# Revit family: Legrand_Atlantic_versione_verticale_riferimenti_036910_a_036950
name_source: partatom
category: Installations électriques
revit_build: Autodesk Revit 2018 (Build: 20170223_1515(x64)
units: mm (PartAtom-declared; Revit-internal decimal feet)

## family parameters
Basée sur le plan de construction = Non
Conserver l'orientation des annotations = Non
Cote de connecteur circulaire = Utiliser le diamètre
Couper avec des vides une fois chargée = Non
Numéro OmniClass = 23.80.00.00
Partagée = Non
Point de calcul de pièce = Non
Titre OmniClass = Electric Power and Lighting
Toujours verticalement = Oui
Type d'élément = Normal

## types (23) — shared parameters
Condizioni Generali di Utilizzo = https://export.legrand.com
ETIM Class 6.0 = EC000058
Fabricant = Legrand
IK = 10
IP = 66
RAL = 7035
URL = www.legrand.fr
materiale = metallo
numero di porte = 1
versione orizzontale = Non
versione quadrata = Non
versione verticale = Oui

## per-type parameters (varying)
- Legrand Atlantic 036913: Scatola 036910=Non; Scatola 036912=Non; Scatola 036913=Oui; Scatola 036917=Non; Scatola 036918=Non; Scatola 036919=Non; Scatola 036920=Non; Scatola 036921=Non; Scatola 036925=Non; Scatola 036926=Non; Scatola 036930=Non; Scatola 036931=Non; Scatola 036932=Non; Scatola 036933=Non; Scatola 036937=Non; Scatola 036938=Non; Scatola 036939=Non; Scatola 036942=Non; Scatola 036943=Non; Scatola 036944=Non; Scatola 036945=Non; Scatola 036946=Non; Scatola 036950=Non; altezza=500 mm  [stored 1.64042 ft]; lunghezza=400 mm  [stored 1.31234 ft]; peso=9.70 kg; profondità=160 mm  [stored 0.524934 ft]
- Legrand Atlantic 036920: Scatola 036910=Non; Scatola 036912=Non; Scatola 036913=Non; Scatola 036917=Non; Scatola 036918=Non; Scatola 036919=Non; Scatola 036920=Oui; Scatola 036921=Non; Scatola 036925=Non; Scatola 036926=Non; Scatola 036930=Non; Scatola 036931=Non; Scatola 036932=Non; Scatola 036933=Non; Scatola 036937=Non; Scatola 036938=Non; Scatola 036939=Non; Scatola 036942=Non; Scatola 036943=Non; Scatola 036944=Non; Scatola 036945=Non; Scatola 036946=Non; Scatola 036950=Non; altezza=600 mm; lunghezza=500 mm  [stored 1.64042 ft]; peso=16.60 kg; profondità=200 mm  [stored 0.656168 ft]
- Legrand Atlantic 036921: Scatola 036910=Non; Scatola 036912=Non; Scatola 036913=Non; Scatola 036917=Non; Scatola 036918=Non; Scatola 036919=Non; Scatola 036920=Non; Scatola 036921=Oui; Scatola 036925=Non; Scatola 036926=Non; Scatola 036930=Non; Scatola 036931=Non; Scatola 036932=Non; Scatola 036933=Non; Scatola 036937=Non; Scatola 036938=Non; Scatola 036939=Non; Scatola 036942=Non; Scatola 036943=Non; Scatola 036944=Non; Scatola 036945=Non; Scatola 036946=Non; Scatola 036950=Non; altezza=700 mm  [stored 2.29659 ft]; lunghezza=500 mm  [stored 1.64042 ft]; peso=18.40 kg; profondità=200 mm  [stored 0.656168 ft]
- Legrand Atlantic 036942: Scatola 036910=Non; Scatola 036912=Non; Scatola 036913=Non; Scatola 036917=Non; Scatola 036918=Non; Scatola 036919=Non; Scatola 036920=Non; Scatola 036921=Non; Scatola 036925=Non; Scatola 036926=Non; Scatola 036930=Non; Scatola 036931=Non; Scatola 036932=Non; Scatola 036933=Non; Scatola 036937=Non; Scatola 036938=Non; Scatola 036939=Non; Scatola 036942=Oui; Scatola 036943=Non; Scatola 036944=Non; Scatola 036945=Non; Scatola 036946=Non; Scatola 036950=Non; altezza=1200 mm; lunghezza=600 mm; peso=47.00 kg; profondità=300 mm
- Legrand Atlantic 036910: Scatola 036910=Oui; Scatola 036912=Non; Scatola 036913=Non; Scatola 036917=Non; Scatola 036918=Non; Scatola 036919=Non; Scatola 036920=Non; Scatola 036921=Non; Scatola 036925=Non; Scatola 036926=Non; Scatola 036930=Non; Scatola 036931=Non; Scatola 036932=Non; Scatola 036933=Non; Scatola 036937=Non; Scatola 036938=Non; Scatola 036939=Non; Scatola 036942=Non; Scatola 036943=Non; Scatola 036944=Non; Scatola 036945=Non; Scatola 036946=Non; Scatola 036950=Non; altezza=300 mm; lunghezza=200 mm  [stored 0.656168 ft]; peso=3.70 kg; profondità=160 mm  [stored 0.524934 ft]
- Legrand Atlantic 036912: Scatola 036910=Non; Scatola 036912=Oui; Scatola 036913=Non; Scatola 036917=Non; Scatola 036918=Non; Scatola 036919=Non; Scatola 036920=Non; Scatola 036921=Non; Scatola 036925=Non; Scatola 036926=Non; Scatola 036930=Non; Scatola 036931=Non; Scatola 036932=Non; Scatola 036933=Non; Scatola 036937=Non; Scatola 036938=Non; Scatola 036939=Non; Scatola 036942=Non; Scatola 036943=Non; Scatola 036944=Non; Scatola 036945=Non; Scatola 036946=Non; Scatola 036950=Non; altezza=400 mm  [stored 1.31234 ft]; lunghezza=300 mm; peso=6.30 kg; profondità=160 mm  [stored 0.524934 ft]
- Legrand Atlantic 036917: Scatola 036910=Non; Scatola 036912=Non; Scatola 036913=Non; Scatola 036917=Oui; Scatola 036918=Non; Scatola 036919=Non; Scatola 036920=Non; Scatola 036921=Non; Scatola 036925=Non; Scatola 036926=Non; Scatola 036930=Non; Scatola 036931=Non; Scatola 036932=Non; Scatola 036933=Non; Scatola 036937=Non; Scatola 036938=Non; Scatola 036939=Non; Scatola 036942=Non; Scatola 036943=Non; Scatola 036944=Non; Scatola 036945=Non; Scatola 036946=Non; Scatola 036950=Non; altezza=400 mm  [stored 1.31234 ft]; lunghezza=300 mm; peso=6.70 kg; profondità=200 mm  [stored 0.656168 ft]
- Legrand Atlantic 036918: Scatola 036910=Non; Scatola 036912=Non; Scatola 036913=Non; Scatola 036917=Non; Scatola 036918=Oui; Scatola 036919=Non; Scatola 036920=Non; Scatola 036921=Non; Scatola 036925=Non; Scatola 036926=Non; Scatola 036930=Non; Scatola 036931=Non; Scatola 036932=Non; Scatola 036933=Non; Scatola 036937=Non; Scatola 036938=Non; Scatola 036939=Non; Scatola 036942=Non; Scatola 036943=Non; Scatola 036944=Non; Scatola 036945=Non; Scatola 036946=Non; Scatola 036950=Non; altezza=500 mm  [stored 1.64042 ft]; lunghezza=400 mm  [stored 1.31234 ft]; peso=10.60 kg; profondità=160 mm  [stored 0.524934 ft]
- Legrand Atlantic 036919: Scatola 036910=Non; Scatola 036912=Non; Scatola 036913=Non; Scatola 036917=Non; Scatola 036918=Non; Scatola 036919=Oui; Scatola 036920=Non; Scatola 036921=Non; Scatola 036925=Non; Scatola 036926=Non; Scatola 036930=Non; Scatola 036931=Non; Scatola 036932=Non; Scatola 036933=Non; Scatola 036937=Non; Scatola 036938=Non; Scatola 036939=Non; Scatola 036942=Non; Scatola 036943=Non; Scatola 036944=Non; Scatola 036945=Non; Scatola 036946=Non; Scatola 036950=Non; altezza=600 mm; lunghezza=400 mm  [stored 1.31234 ft]; peso=12.00 kg; profondità=160 mm  [stored 0.524934 ft]
- Legrand Atlantic 036925: Scatola 036910=Non; Scatola 036912=Non; Scatola 036913=Non; Scatola 036917=Non; Scatola 036918=Non; Scatola 036919=Non; Scatola 036920=Non; Scatola 036921=Non; Scatola 036925=Oui; Scatola 036926=Non; Scatola 036930=Non; Scatola 036931=Non; Scatola 036932=Non; Scatola 036933=Non; Scatola 036937=Non; Scatola 036938=Non; Scatola 036939=Non; Scatola 036942=Non; Scatola 036943=Non; Scatola 036944=Non; Scatola 036945=Non; Scatola 036946=Non; Scatola 036950=Non; altezza=500 mm  [stored 1.64042 ft]; lunghezza=400 mm  [stored 1.31234 ft]; peso=11.30 kg; profondità=250 mm  [stored 0.82021 ft]
- Legrand Atlantic 036926: Scatola 036910=Non; Scatola 036912=Non; Scatola 036913=Non; Scatola 036917=Non; Scatola 036918=Non; Scatola 036919=Non; Scatola 036920=Non; Scatola 036921=Non; Scatola 036925=Non; Scatola 036926=Oui; Scatola 036930=Non; Scatola 036931=Non; Scatola 036932=Non; Scatola 036933=Non; Scatola 036937=Non; Scatola 036938=Non; Scatola 036939=Non; Scatola 036942=Non; Scatola 036943=Non; Scatola 036944=Non; Scatola 036945=Non; Scatola 036946=Non; Scatola 036950=Non; altezza=500 mm  [stored 1.64042 ft]; lunghezza=400 mm  [stored 1.31234 ft]; peso=12.80 kg; profondità=250 mm  [stored 0.82021 ft]
- Legrand Atlantic 036930: Scatola 036910=Non; Scatola 036912=Non; Scatola 036913=Non; Scatola 036917=Non; Scatola 036918=Non; Scatola 036919=Non; Scatola 036920=Non; Scatola 036921=Non; Scatola 036925=Non; Scatola 036926=Non; Scatola 036930=Oui; Scatola 036931=Non; Scatola 036932=Non; Scatola 036933=Non; Scatola 036937=Non; Scatola 036938=Non; Scatola 036939=Non; Scatola 036942=Non; Scatola 036943=Non; Scatola 036944=Non; Scatola 036945=Non; Scatola 036946=Non; Scatola 036950=Non; altezza=700 mm  [stored 2.29659 ft]; lunghezza=500 mm  [stored 1.64042 ft]; peso=19.60 kg; profondità=250 mm  [stored 0.82021 ft]
- Legrand Atlantic 036931: Scatola 036910=Non; Scatola 036912=Non; Scatola 036913=Non; Scatola 036917=Non; Scatola 036918=Non; Scatola 036919=Non; Scatola 036920=Non; Scatola 036921=Non; Scatola 036925=Non; Scatola 036926=Non; Scatola 036930=Non; Scatola 036931=Oui; Scatola 036932=Non; Scatola 036933=Non; Scatola 036937=Non; Scatola 036938=Non; Scatola 036939=Non; Scatola 036942=Non; Scatola 036943=Non; Scatola 036944=Non; Scatola 036945=Non; Scatola 036946=Non; Scatola 036950=Non; altezza=800 mm  [stored 2.62467 ft]; lunghezza=600 mm; peso=26.60 kg; profondità=250 mm  [stored 0.82021 ft]
- Legrand Atlantic 036932: Scatola 036910=Non; Scatola 036912=Non; Scatola 036913=Non; Scatola 036917=Non; Scatola 036918=Non; Scatola 036919=Non; Scatola 036920=Non; Scatola 036921=Non; Scatola 036925=Non; Scatola 036926=Non; Scatola 036930=Non; Scatola 036931=Non; Scatola 036932=Oui; Scatola 036933=Non; Scatola 036937=Non; Scatola 036938=Non; Scatola 036939=Non; Scatola 036942=Non; Scatola 036943=Non; Scatola 036944=Non; Scatola 036945=Non; Scatola 036946=Non; Scatola 036950=Non; altezza=1000 mm  [stored 3.28084 ft]; lunghezza=600 mm; peso=36.20 kg; profondità=250 mm  [stored 0.82021 ft]
- Legrand Atlantic 036933: Scatola 036910=Non; Scatola 036912=Non; Scatola 036913=Non; Scatola 036917=Non; Scatola 036918=Non; Scatola 036919=Non; Scatola 036920=Non; Scatola 036921=Non; Scatola 036925=Non; Scatola 036926=Non; Scatola 036930=Non; Scatola 036931=Non; Scatola 036932=Non; Scatola 036933=Oui; Scatola 036937=Non; Scatola 036938=Non; Scatola 036939=Non; Scatola 036942=Non; Scatola 036943=Non; Scatola 036944=Non; Scatola 036945=Non; Scatola 036946=Non; Scatola 036950=Non; altezza=1000 mm  [stored 3.28084 ft]; lunghezza=800 mm  [stored 2.62467 ft]; peso=46.80 kg; profondità=250 mm  [stored 0.82021 ft]
- Legrand Atlantic 036937: Scatola 036910=Non; Scatola 036912=Non; Scatola 036913=Non; Scatola 036917=Non; Scatola 036918=Non; Scatola 036919=Non; Scatola 036920=Non; Scatola 036921=Non; Scatola 036925=Non; Scatola 036926=Non; Scatola 036930=Non; Scatola 036931=Non; Scatola 036932=Non; Scatola 036933=Non; Scatola 036937=Oui; Scatola 036938=Non; Scatola 036939=Non; Scatola 036942=Non; Scatola 036943=Non; Scatola 036944=Non; Scatola 036945=Non; Scatola 036946=Non; Scatola 036950=Non; altezza=800 mm  [stored 2.62467 ft]; lunghezza=600 mm; peso=28.80 kg; profondità=300 mm
- Legrand Atlantic 036938: Scatola 036910=Non; Scatola 036912=Non; Scatola 036913=Non; Scatola 036917=Non; Scatola 036918=Non; Scatola 036919=Non; Scatola 036920=Non; Scatola 036921=Non; Scatola 036925=Non; Scatola 036926=Non; Scatola 036930=Non; Scatola 036931=Non; Scatola 036932=Non; Scatola 036933=Non; Scatola 036937=Non; Scatola 036938=Oui; Scatola 036939=Non; Scatola 036942=Non; Scatola 036943=Non; Scatola 036944=Non; Scatola 036945=Non; Scatola 036946=Non; Scatola 036950=Non; altezza=1000 mm  [stored 3.28084 ft]; lunghezza=600 mm; peso=37.80 kg; profondità=300 mm
- Legrand Atlantic 036939: Scatola 036910=Non; Scatola 036912=Non; Scatola 036913=Non; Scatola 036917=Non; Scatola 036918=Non; Scatola 036919=Non; Scatola 036920=Non; Scatola 036921=Non; Scatola 036925=Non; Scatola 036926=Non; Scatola 036930=Non; Scatola 036931=Non; Scatola 036932=Non; Scatola 036933=Non; Scatola 036937=Non; Scatola 036938=Non; Scatola 036939=Oui; Scatola 036942=Non; Scatola 036943=Non; Scatola 036944=Non; Scatola 036945=Non; Scatola 036946=Non; Scatola 036950=Non; altezza=1000 mm  [stored 3.28084 ft]; lunghezza=800 mm  [stored 2.62467 ft]; peso=50.50 kg; profondità=300 mm
- Legrand Atlantic 036943: Scatola 036910=Non; Scatola 036912=Non; Scatola 036913=Non; Scatola 036917=Non; Scatola 036918=Non; Scatola 036919=Non; Scatola 036920=Non; Scatola 036921=Non; Scatola 036925=Non; Scatola 036926=Non; Scatola 036930=Non; Scatola 036931=Non; Scatola 036932=Non; Scatola 036933=Non; Scatola 036937=Non; Scatola 036938=Non; Scatola 036939=Non; Scatola 036942=Non; Scatola 036943=Oui; Scatola 036944=Non; Scatola 036945=Non; Scatola 036946=Non; Scatola 036950=Non; altezza=1200 mm; lunghezza=800 mm  [stored 2.62467 ft]; peso=62.20 kg; profondità=300 mm
- Legrand Atlantic 036944: Scatola 036910=Non; Scatola 036912=Non; Scatola 036913=Non; Scatola 036917=Non; Scatola 036918=Non; Scatola 036919=Non; Scatola 036920=Non; Scatola 036921=Non; Scatola 036925=Non; Scatola 036926=Non; Scatola 036930=Non; Scatola 036931=Non; Scatola 036932=Non; Scatola 036933=Non; Scatola 036937=Non; Scatola 036938=Non; Scatola 036939=Non; Scatola 036942=Non; Scatola 036943=Non; Scatola 036944=Oui; Scatola 036945=Non; Scatola 036946=Non; Scatola 036950=Non; altezza=800 mm  [stored 2.62467 ft]; lunghezza=600 mm; peso=36.80 kg; profondità=400 mm  [stored 1.31234 ft]
- Legrand Atlantic 036945: Scatola 036910=Non; Scatola 036912=Non; Scatola 036913=Non; Scatola 036917=Non; Scatola 036918=Non; Scatola 036919=Non; Scatola 036920=Non; Scatola 036921=Non; Scatola 036925=Non; Scatola 036926=Non; Scatola 036930=Non; Scatola 036931=Non; Scatola 036932=Non; Scatola 036933=Non; Scatola 036937=Non; Scatola 036938=Non; Scatola 036939=Non; Scatola 036942=Non; Scatola 036943=Non; Scatola 036944=Non; Scatola 036945=Oui; Scatola 036946=Non; Scatola 036950=Non; altezza=1000 mm  [stored 3.28084 ft]; lunghezza=800 mm  [stored 2.62467 ft]; peso=62.30 kg; profondità=400 mm  [stored 1.31234 ft]
- Legrand Atlantic 036946: Scatola 036910=Non; Scatola 036912=Non; Scatola 036913=Non; Scatola 036917=Non; Scatola 036918=Non; Scatola 036919=Non; Scatola 036920=Non; Scatola 036921=Non; Scatola 036925=Non; Scatola 036926=Non; Scatola 036930=Non; Scatola 036931=Non; Scatola 036932=Non; Scatola 036933=Non; Scatola 036937=Non; Scatola 036938=Non; Scatola 036939=Non; Scatola 036942=Non; Scatola 036943=Non; Scatola 036944=Non; Scatola 036945=Non; Scatola 036946=Oui; Scatola 036950=Non; altezza=1200 mm; lunghezza=800 mm  [stored 2.62467 ft]; peso=76.00 kg; profondità=400 mm  [stored 1.31234 ft]
- Legrand Atlantic 036950: Scatola 036910=Non; Scatola 036912=Non; Scatola 036913=Non; Scatola 036917=Non; Scatola 036918=Non; Scatola 036919=Non; Scatola 036920=Non; Scatola 036921=Non; Scatola 036925=Non; Scatola 036926=Non; Scatola 036930=Non; Scatola 036931=Non; Scatola 036932=Non; Scatola 036933=Non; Scatola 036937=Non; Scatola 036938=Non; Scatola 036939=Non; Scatola 036942=Non; Scatola 036943=Non; Scatola 036944=Non; Scatola 036945=Non; Scatola 036946=Non; Scatola 036950=Oui; altezza=1400 mm  [stored 4.59318 ft]; lunghezza=800 mm  [stored 2.62467 ft]; peso=80.90 kg; profondità=400 mm  [stored 1.31234 ft]

note: column(s) folded — value = type name in every type: Description

note: [stored X ft] marks values corroborated as IEEE doubles in the binary element streams (Revit-internal decimal feet)
